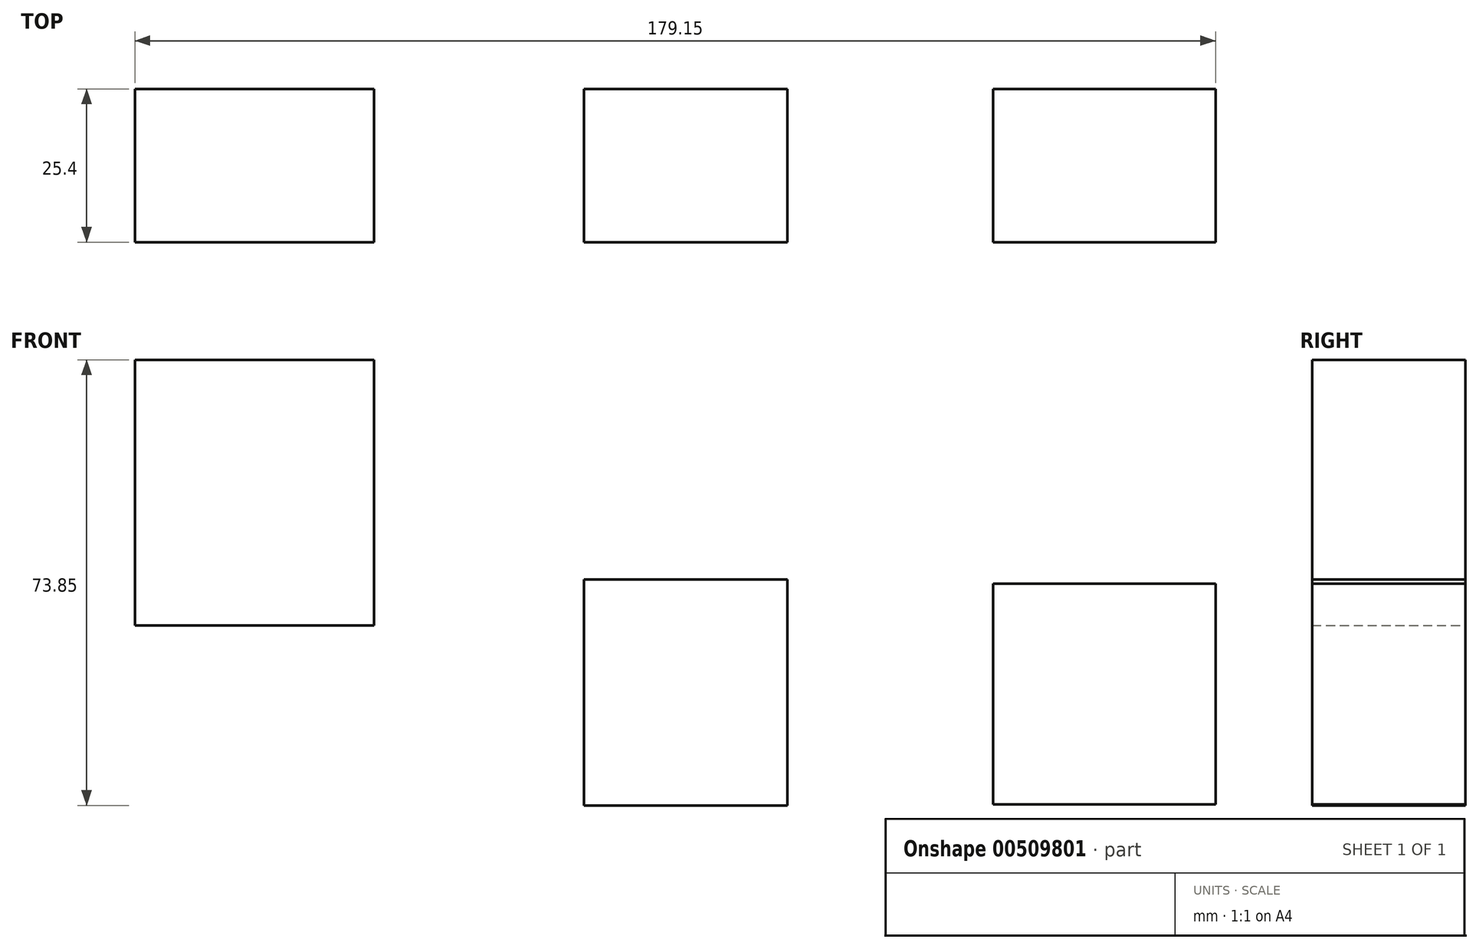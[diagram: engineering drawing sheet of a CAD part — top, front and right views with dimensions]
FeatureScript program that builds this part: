
annotation { "Feature Type Name" : "Feature", "Feature Type Description" : "" }
export const myFeature = defineFeature(function(context is Context, id is Id, definition is map)
    precondition{}
    {
        {
            var Q0;
            Q0=qCreatedBy(makeId("Front.planeOp"),FACE);
            var sketch = newSketch(context, id + "F0", { "sketchPlane" : qUnion([Q0])});
            skLineSegment(sketch, "E0.bottom", {"start": v(-100.67, 50.6) * mm, "end": v(-61.05, 50.6) * mm});
            skLineSegment(sketch, "E0.top", {"start": v(-100.67, 6.57) * mm, "end": v(-61.05, 6.57) * mm});
            skLineSegment(sketch, "E0.left", {"start": v(-100.67, 50.6) * mm, "end": v(-100.67, 6.57) * mm});
            skLineSegment(sketch, "E0.right", {"start": v(-61.05, 50.6) * mm, "end": v(-61.05, 6.57) * mm});
            skLineSegment(sketch, "E1.bottom", {"start": v(-26.25, 14.2) * mm, "end": v(7.51, 14.2) * mm});
            skLineSegment(sketch, "E1.top", {"start": v(-26.25, -23.25) * mm, "end": v(7.51, -23.25) * mm});
            skLineSegment(sketch, "E1.left", {"start": v(-26.25, 14.2) * mm, "end": v(-26.25, -23.25) * mm});
            skLineSegment(sketch, "E1.right", {"start": v(7.51, 14.2) * mm, "end": v(7.51, -23.25) * mm});
            skLineSegment(sketch, "E2.bottom", {"start": v(41.62, 13.47) * mm, "end": v(78.48, 13.47) * mm});
            skLineSegment(sketch, "E2.top", {"start": v(41.62, -23.09) * mm, "end": v(78.48, -23.09) * mm});
            skLineSegment(sketch, "E2.left", {"start": v(41.62, 13.47) * mm, "end": v(41.62, -23.09) * mm});
            skLineSegment(sketch, "E2.right", {"start": v(78.48, 13.47) * mm, "end": v(78.48, -23.09) * mm});
            skSolve(sketch);
        }
        {
            var Q0;
            Q0 = qSketchRegion(id + "F0", true);
            extrude(context, id + "F1", {"entities" : qUnion([Q0]), "depth" : 25.4 * mm});
        }
    });
